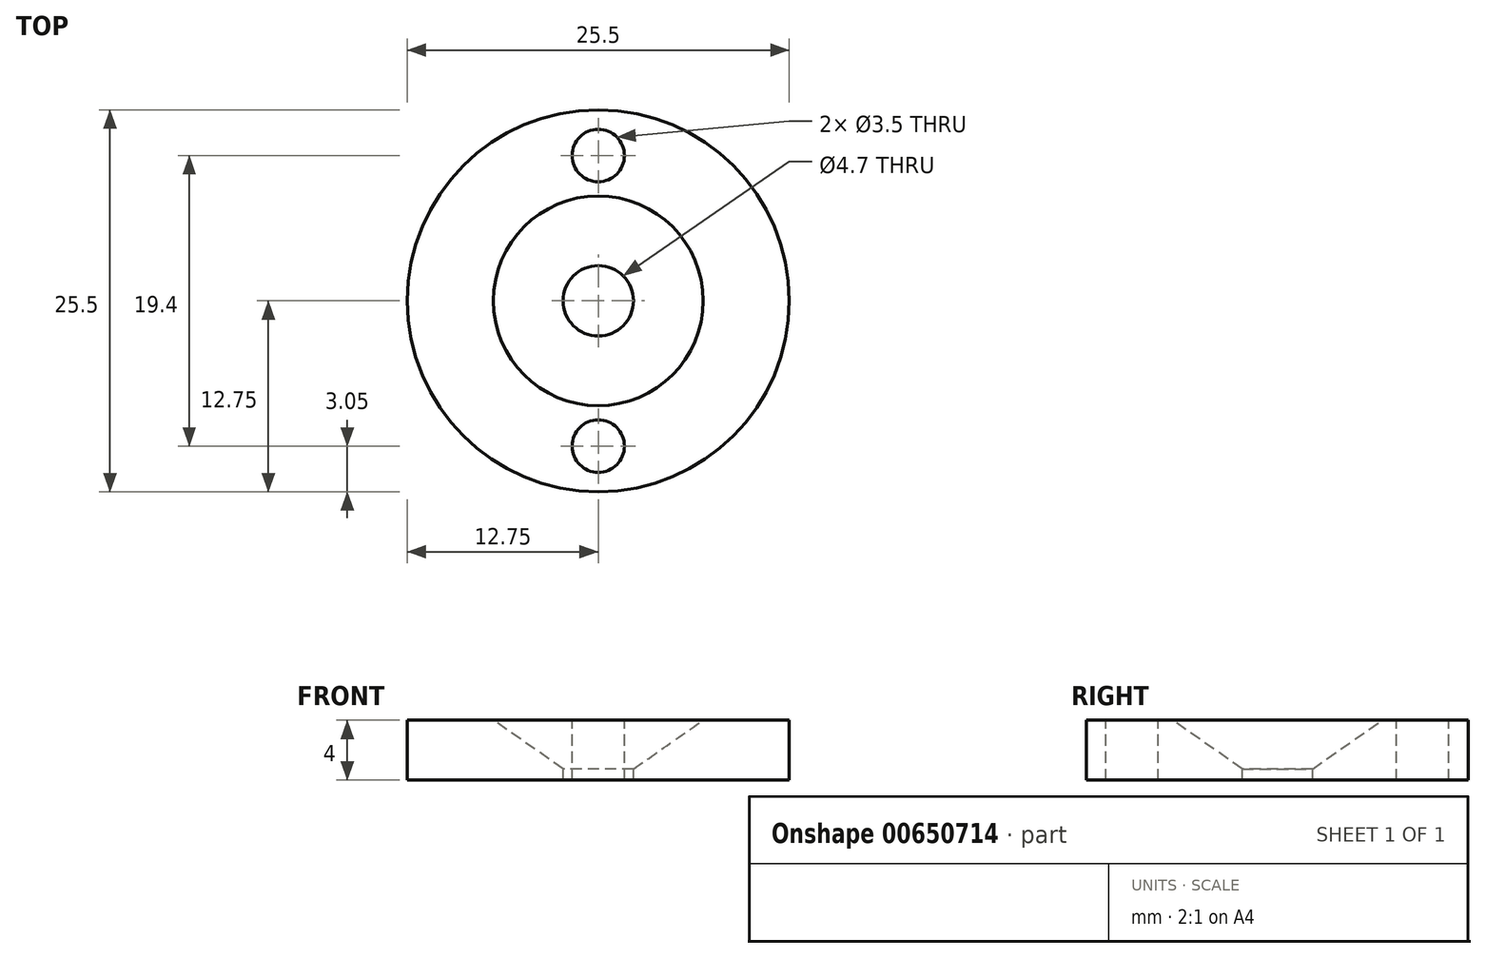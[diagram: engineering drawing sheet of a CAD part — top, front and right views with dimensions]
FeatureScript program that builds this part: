
annotation { "Feature Type Name" : "Feature", "Feature Type Description" : "" }
export const myFeature = defineFeature(function(context is Context, id is Id, definition is map)
    precondition{}
    {
        {
            var Q0;
            Q0=qCreatedBy(makeId("Top.planeOp"),FACE);
            var sketch = newSketch(context, id + "F0", { "sketchPlane" : qUnion([Q0])});
            skCircle(sketch, "E0", {"center": v(0, 0) * mm, "radius": 12.75 * mm});
            skSolve(sketch);
        }
        {
            var Q0;
            Q0 = qSketchRegion(id + "F0", true);
            extrude(context, id + "F1", {"entities" : qUnion([Q0]), "depth" : 4 * mm, "offsetDistance" : 25 * mm});
        }
        {
            var Q0;
            Q0=makeQuery(id+"F1.opExtrude","CAP_FACE",FACE,{"disambiguationData":[OSD([sQuery(id+"F0.wireOp",EDGE,"E0")])],"isStart":false});
            var sketch = newSketch(context, id + "F2", { "sketchPlane" : qUnion([Q0])});
            skPoint(sketch, "E1", {"position": v(0, 0) * mm});
            skSolve(sketch);
        }
        {
            var Q0;
            Q0=sQuery(id+"F2.wireOp",VERTEX,"E1");
            var Q1;
            Q1=makeQuery(id+"F1.opExtrude","SWEPT_BODY",BODY,{"disambiguationData":[OSD([sQuery(id+"F0.wireOp",EDGE,"E0")])]});
            hole(context, id + "F3", {"style" : HoleStyle.C_SINK, "endStyle" : HoleEndStyle.THROUGH, "holeDiameter" : 4.7 * mm, "cSinkDiameter" : 14 * mm, "cSinkAngle" : 110 * degree, "majorDiameter" : 5 * mm, "isTappedThrough" : true, "tappedDepth" : 12 * mm, "tapClearance" : 3, "locations" : qUnion([Q0]), "scope" : qUnion([Q1])});
        }
        {
            var Q0;
            Q0=makeQuery(id+"F1.opExtrude","CAP_FACE",FACE,{"disambiguationData":[OSD([sQuery(id+"F0.wireOp",EDGE,"E0")])],"isStart":false});
            var sketch = newSketch(context, id + "F4", { "sketchPlane" : qUnion([Q0])});
            skCircle(sketch, "E2", {"center": v(0, -9.7) * mm, "radius": 1.75 * mm});
            skCircle(sketch, "E3", {"center": v(0, 9.7) * mm, "radius": 1.75 * mm});
            skSolve(sketch);
        }
        {
            var Q0;
            Q0 = qSketchRegion(id + "F4", true);
            extrude(context, id + "F5", {"entities" : qUnion([Q0]), "operationType" : NewBodyOperationType.REMOVE, "endBound" : BoundingType.THROUGH_ALL, "oppositeDirection" : true, "depth" : 25 * mm, "offsetDistance" : 25 * mm});
        }
    });
